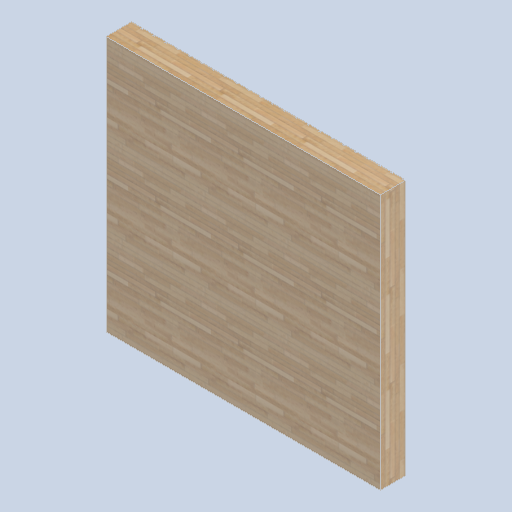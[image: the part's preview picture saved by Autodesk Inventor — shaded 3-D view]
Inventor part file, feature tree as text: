
AUTODESK INVENTOR PART (.ipt)
format: ipt  version: 2024.2 (Build 282272000, 272)  size: 377,344 bytes
history: native  units: in
note: dims shown in document units (in); Inventor stores cm internally (conversion verified against a paired STEP export)
features: other x3, sketch x1
ambient origin geometry x8: Origin, YZ Plane, XZ Plane, XY Plane, X Axis, Y Axis, Z Axis, Center Point
bodies: Solid1 (feature_tree)
feature tree (4):
  other  "front_wall_block05.ipt"
  other  "Solid1::front_wall_block05.ipt"
  other  "TaggingFeature1"
  sketch  "Sketch3"  dims[d0=0.3937in]
